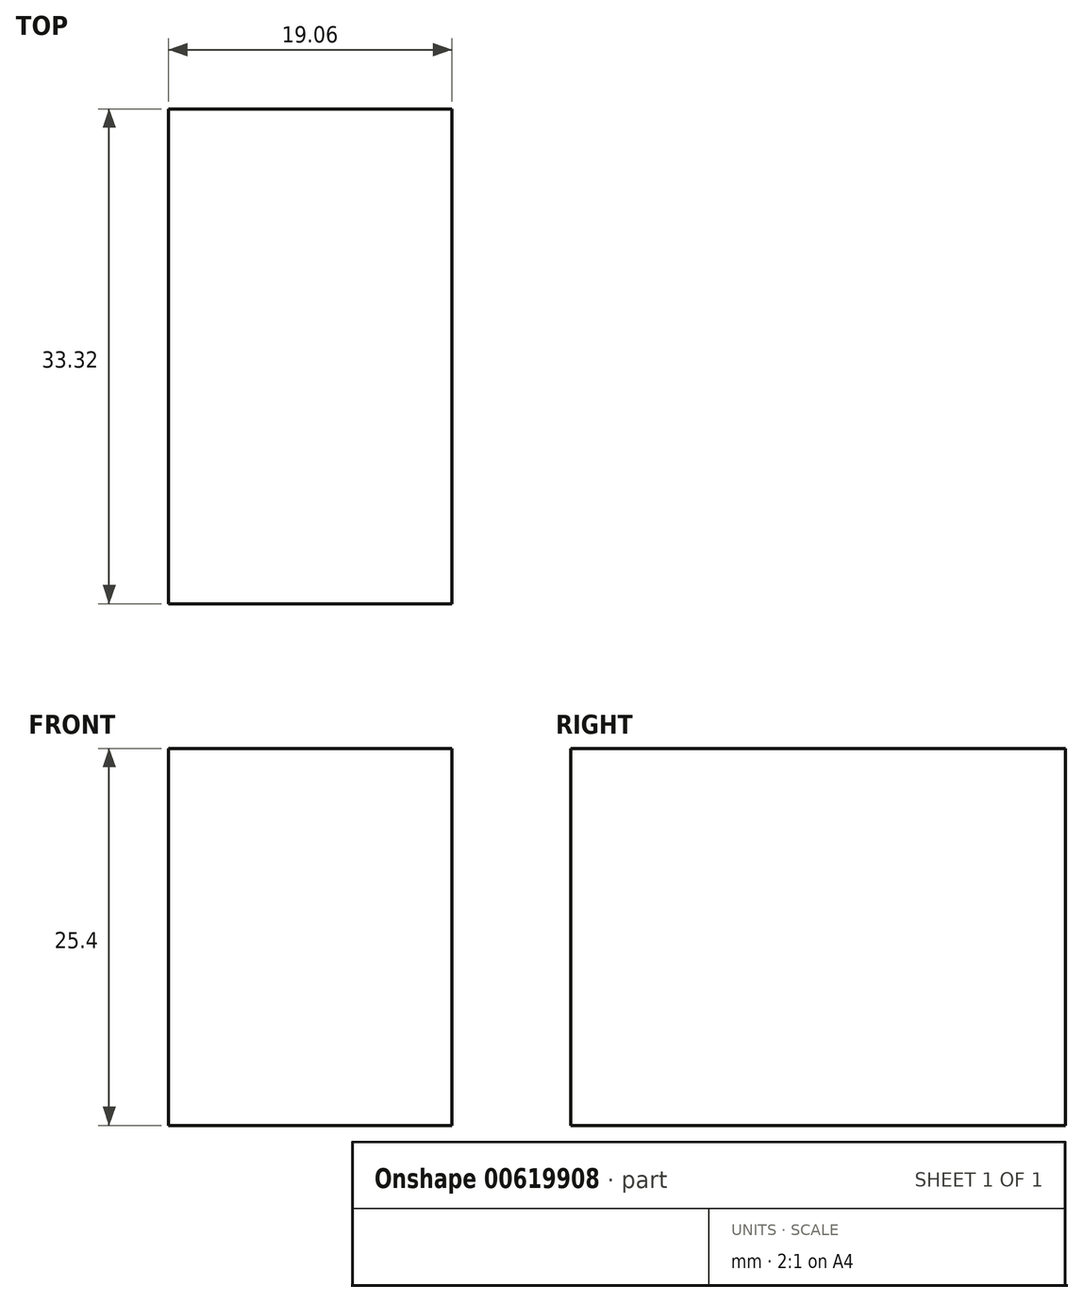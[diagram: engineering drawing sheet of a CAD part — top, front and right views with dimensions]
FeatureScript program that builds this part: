
annotation { "Feature Type Name" : "Feature", "Feature Type Description" : "" }
export const myFeature = defineFeature(function(context is Context, id is Id, definition is map)
    precondition{}
    {
        {
            var Q0;
            Q0=qCreatedBy(makeId("Top.planeOp"),FACE);
            var sketch = newSketch(context, id + "F0", { "sketchPlane" : qUnion([Q0])});
            skLineSegment(sketch, "E0.bottom", {"start": v(0, 0) * mm, "end": v(19.06, 0) * mm});
            skLineSegment(sketch, "E0.top", {"start": v(0, 33.32) * mm, "end": v(19.06, 33.32) * mm});
            skLineSegment(sketch, "E0.left", {"start": v(0, 0) * mm, "end": v(0, 33.32) * mm});
            skLineSegment(sketch, "E0.right", {"start": v(19.06, 0) * mm, "end": v(19.06, 33.32) * mm});
            skSolve(sketch);
        }
        {
            var Q0;
            Q0=makeQuery(id+"F0.imprint","IMPRINT",FACE,{"disambiguationData":[TD([[makeQuery(id+"F0.imprint","IMPRINT",EDGE,{"derivedFrom":sQuery(id+"F0.wireOp",EDGE,"E0.bottom")}),1.0]])]});
            extrude(context, id + "F1", {"entities" : qUnion([Q0]), "depth" : 25.4 * mm, "offsetDistance" : 25.4 * mm});
        }
    });
